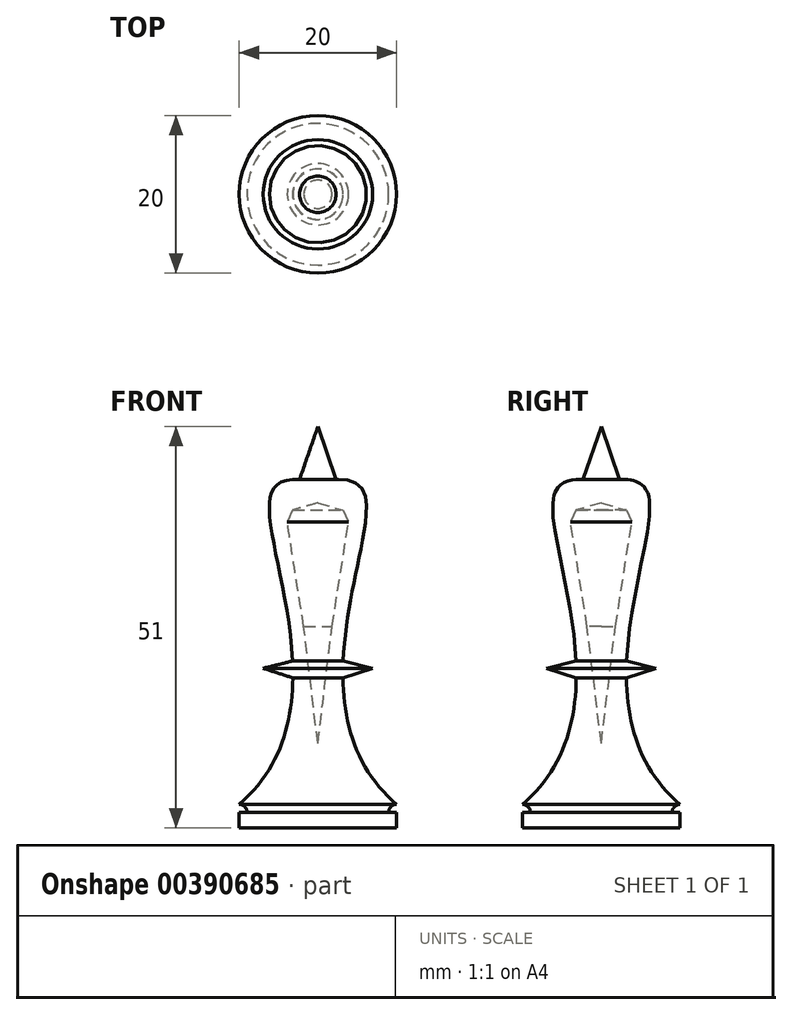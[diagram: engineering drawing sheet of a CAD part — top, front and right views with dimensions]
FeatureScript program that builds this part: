
annotation { "Feature Type Name" : "Feature", "Feature Type Description" : "" }
export const myFeature = defineFeature(function(context is Context, id is Id, definition is map)
    precondition{}
    {
        {
            var Q0;
            Q0=qCreatedBy(makeId("Front.planeOp"),FACE);
            var sketch = newSketch(context, id + "F0", { "sketchPlane" : qUnion([Q0])});
            skLineSegment(sketch, "E0", {"start": v(0, 0) * mm, "end": v(10, 0) * mm});
            skLineSegment(sketch, "E1", {"start": v(10, 0) * mm, "end": v(10, 2) * mm});
            skLineSegment(sketch, "E2", {"start": v(10, 2) * mm, "end": v(9, 2) * mm});
            skPoint(sketch, "E3.endSnap0", {"position": v(10, 1) * mm});
            skArc(sketch, "E4", {"start": v(9, 2) * mm, "mid": v(9.3, 2.7) * mm, "end": v(10, 3) * mm});
            skFitSpline(sketch, "E5", {"points": [v(10, 3) * mm, v(6.16, 40.18) * mm, v(0, 44) * mm], "startDerivative": vector(-53.43, 45.76) * mm, "endDerivative": vector(-48.65, -9.12) * mm});
            skLineSegment(sketch, "E6", {"start": v(0, 0) * mm, "end": v(0, 44) * mm});
            skLineSegment(sketch, "E7", {"start": v(0, 44) * mm, "end": v(0, 51) * mm});
            skPoint(sketch, "E8.endSnap0", {"position": v(0, 22) * mm});
            skLineSegment(sketch, "E9", {"start": v(0, 22) * mm, "end": v(6.95, 20.28) * mm});
            skLineSegment(sketch, "E10", {"start": v(6.95, 20.28) * mm, "end": v(0, 18.04) * mm});
            skLineSegment(sketch, "E11", {"start": v(0, 51) * mm, "end": v(3.33, 41.33) * mm});
            skLineSegment(sketch, "E12", {"start": v(0, 41.3) * mm, "end": v(3.22, 40.38) * mm});
            skLineSegment(sketch, "E13", {"start": v(3.22, 40.38) * mm, "end": v(3.9, 38.87) * mm});
            skLineSegment(sketch, "E14", {"start": v(3.9, 38.87) * mm, "end": v(1.8, 25.57) * mm});
            skLineSegment(sketch, "E15", {"start": v(1.8, 25.57) * mm, "end": v(0, 10.76) * mm});
            skSolve(sketch);
        }
        {
            var Q0;
            {var subQ0=sQuery(id+"F0.wireOp",EDGE,"E0");Q0=makeQuery(id+"F0.imprint","IMPRINT",FACE,{"disambiguationData":[TD([[makeQuery(id+"F0.imprint","IMPRINT",EDGE,{"derivedFrom":subQ0}),1.0]])]});}
            var Q1;
            {var subQ0=sQuery(id+"F0.wireOp",EDGE,"E7");Q1=makeQuery(id+"F0.imprint","IMPRINT",FACE,{"disambiguationData":[TD([[makeQuery(id+"F0.imprint","IMPRINT",EDGE,{"derivedFrom":subQ0}),-1.0]])]});}
            var Q2;
            {var subQ0=sQuery(id+"F0.wireOp",EDGE,"E6");var subQ3=sQuery(id+"F0.wireOp",EDGE,"UrGRKQzg-VSOa-ZteD-O5Gp-x69Zk8rxus1x");var subQ5=makeQuery(id+"F0.imprint","INTERSECT",VERTEX,{"derivedFrom":[subQ0,subQ3]});Q2=makeQuery(id+"F0.imprint","IMPRINT",FACE,{"disambiguationData":[TD([[makeQuery(id+"F0.imprint","IMPRINT",EDGE,{"disambiguationData":[TD([[subQ5,-1.0]])],"derivedFrom":subQ3}),1.0]])]});}
            var Q3;
            {var subQ0=sQuery(id+"F0.wireOp",EDGE,"E10");var subQ1=sQuery(id+"F0.wireOp",EDGE,"E5");var subQ2=makeQuery(id+"F0.imprint","INTERSECT",VERTEX,{"derivedFrom":[subQ1,subQ0]});Q3=makeQuery(id+"F0.imprint","IMPRINT",FACE,{"disambiguationData":[TD([[makeQuery(id+"F0.imprint","IMPRINT",EDGE,{"disambiguationData":[TD([[subQ2,-1.0]])],"derivedFrom":subQ1}),1.0]])]});}
            var Q4;
            {var subQ0=sQuery(id+"F0.wireOp",EDGE,"E10");var subQ1=sQuery(id+"F0.wireOp",EDGE,"E5");var subQ2=makeQuery(id+"F0.imprint","INTERSECT",VERTEX,{"derivedFrom":[subQ1,subQ0]});Q4=makeQuery(id+"F0.imprint","IMPRINT",FACE,{"disambiguationData":[TD([[makeQuery(id+"F0.imprint","IMPRINT",EDGE,{"disambiguationData":[TD([[subQ2,-1.0]])],"derivedFrom":subQ1}),-1.0]])]});}
            var Q5;
            {var subQ0=sQuery(id+"F0.wireOp",EDGE,"E9");var subQ1=sQuery(id+"F0.wireOp",EDGE,"E5");var subQ2=makeQuery(id+"F0.imprint","INTERSECT",VERTEX,{"derivedFrom":[subQ1,subQ0]});Q5=makeQuery(id+"F0.imprint","IMPRINT",FACE,{"disambiguationData":[TD([[makeQuery(id+"F0.imprint","IMPRINT",EDGE,{"disambiguationData":[TD([[subQ2,-1.0]])],"derivedFrom":subQ1}),1.0]])]});}
            var Q6;
            Q6=sQuery(id+"F0.wireOp",EDGE,"E6");
            revolve(context, id + "F1", {"entities" : qUnion([Q0, Q1, Q2, Q3, Q4, Q5]), "axis" : qUnion([Q6]), "revolveType" : RevolveType.FULL});
        }
    });
